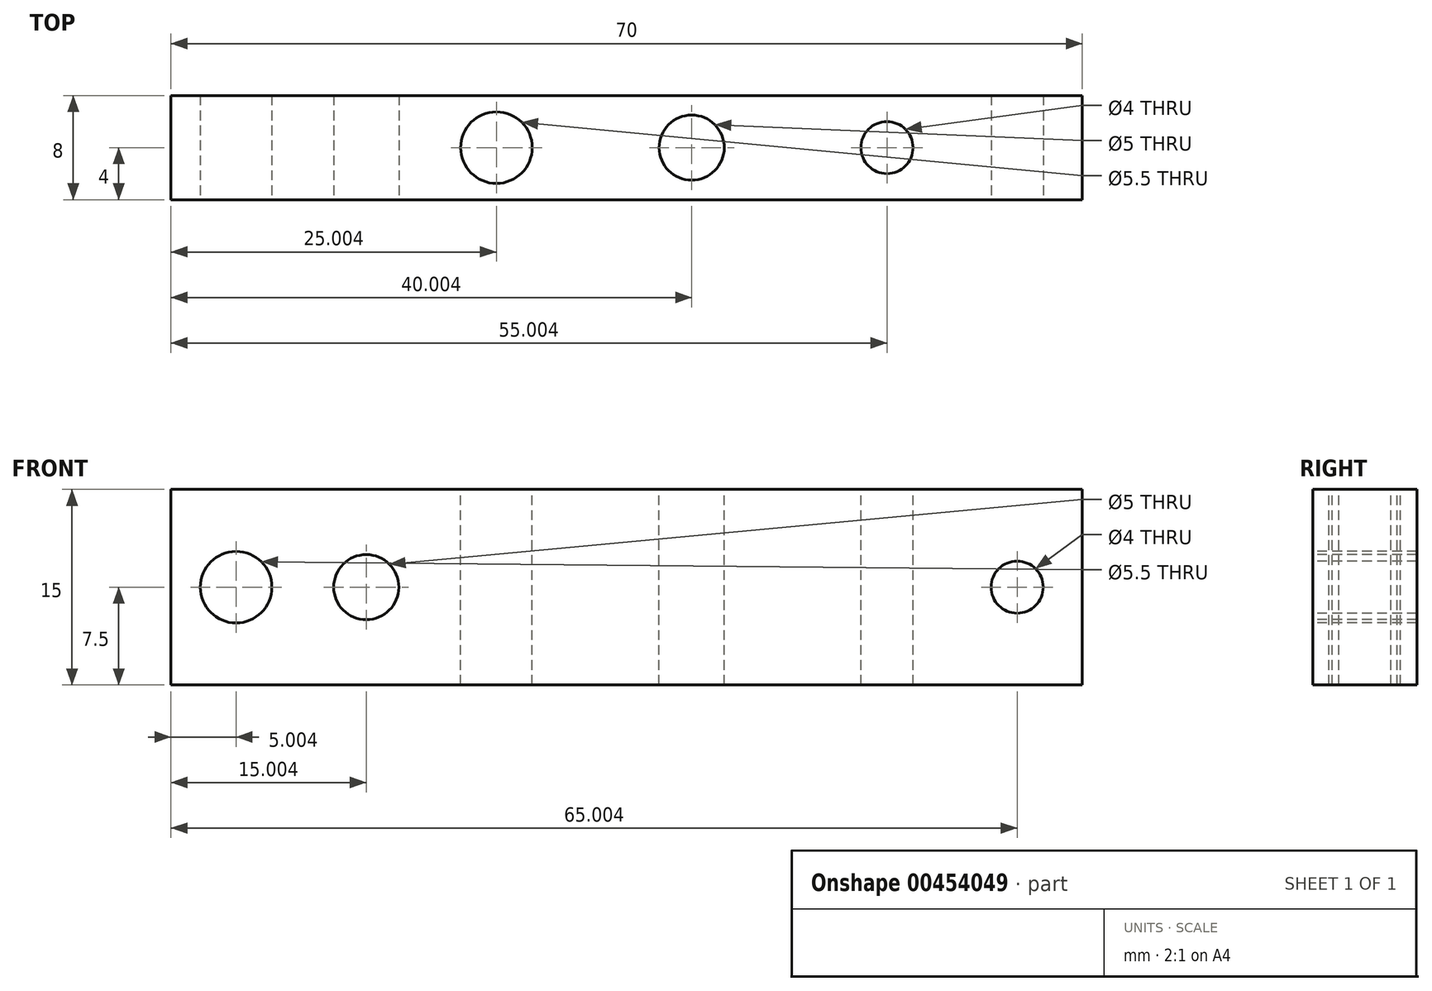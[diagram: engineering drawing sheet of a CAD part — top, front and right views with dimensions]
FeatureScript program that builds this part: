
annotation { "Feature Type Name" : "Feature", "Feature Type Description" : "" }
export const myFeature = defineFeature(function(context is Context, id is Id, definition is map)
    precondition{}
    {
        {
            var Q0;
            Q0=qCreatedBy(makeId("Top.planeOp"),FACE);
            var sketch = newSketch(context, id + "F0", { "sketchPlane" : qUnion([Q0])});
            skLineSegment(sketch, "E0.bottom", {"start": v(-4682.17, -4679.78) * mm, "end": v(-4612.17, -4679.78) * mm});
            skLineSegment(sketch, "E0.top", {"start": v(-4682.17, -4687.78) * mm, "end": v(-4612.17, -4687.78) * mm});
            skLineSegment(sketch, "E0.left", {"start": v(-4682.17, -4679.78) * mm, "end": v(-4682.17, -4687.78) * mm});
            skLineSegment(sketch, "E0.right", {"start": v(-4612.17, -4679.78) * mm, "end": v(-4612.17, -4687.78) * mm});
            skSolve(sketch);
        }
        {
            var Q0;
            Q0 = qSketchRegion(id + "F0", true);
            extrude(context, id + "F1", {"entities" : qUnion([Q0]), "depth" : 15 * mm, "offsetDistance" : 25 * mm});
        }
        {
            var Q0;
            Q0=makeQuery(id+"F1.opExtrude","SWEPT_FACE",FACE,{"disambiguationData":[OSD([sQuery(id+"F0.wireOp",EDGE,"E0.top")])]});
            var sketch = newSketch(context, id + "F2", { "sketchPlane" : qUnion([Q0])});
            skCircle(sketch, "E1", {"center": v(-4677.17, 7.5) * mm, "radius": 2.75 * mm});
            skCircle(sketch, "E2", {"center": v(-4617.17, 7.5) * mm, "radius": 2 * mm});
            skCircle(sketch, "E3", {"center": v(-4667.17, 7.5) * mm, "radius": 2.5 * mm});
            skSolve(sketch);
        }
        {
            var Q0;
            Q0 = qSketchRegion(id + "F2", true);
            extrude(context, id + "F3", {"entities" : qUnion([Q0]), "operationType" : NewBodyOperationType.REMOVE, "oppositeDirection" : true, "depth" : 8 * mm, "offsetDistance" : 25 * mm});
        }
        {
            var Q0;
            Q0=makeQuery(id+"F1.opExtrude","CAP_FACE",FACE,{"disambiguationData":[OSD([sQuery(id+"F0.wireOp",EDGE,"E0.bottom"),sQuery(id+"F0.wireOp",EDGE,"E0.top"),sQuery(id+"F0.wireOp",EDGE,"E0.left"),sQuery(id+"F0.wireOp",EDGE,"E0.right")])],"isStart":false});
            var sketch = newSketch(context, id + "F4", { "sketchPlane" : qUnion([Q0])});
            skCircle(sketch, "E4", {"center": v(-4657.17, -4683.78) * mm, "radius": 2.75 * mm});
            skCircle(sketch, "E5", {"center": v(-4642.17, -4683.78) * mm, "radius": 2.5 * mm});
            skCircle(sketch, "E6", {"center": v(-4627.17, -4683.78) * mm, "radius": 2 * mm});
            skSolve(sketch);
        }
        {
            var Q0;
            Q0 = qSketchRegion(id + "F4", true);
            extrude(context, id + "F5", {"entities" : qUnion([Q0]), "operationType" : NewBodyOperationType.REMOVE, "oppositeDirection" : true, "depth" : 25 * mm, "offsetDistance" : 25 * mm});
        }
    });
